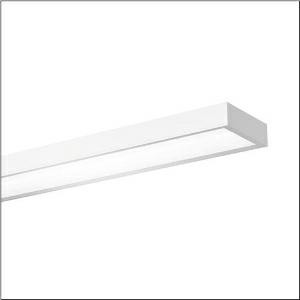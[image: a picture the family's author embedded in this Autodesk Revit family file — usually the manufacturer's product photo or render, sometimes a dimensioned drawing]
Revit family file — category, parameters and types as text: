
# Revit family: sport_31_51hs12dc4dca
name_source: partatom
category: Lighting Fixtures
units: mm (PartAtom-declared; Revit-internal decimal feet)

## family parameters
Cut with Voids When Loaded = No
Host = Face
Light Source = No
Part Type = Normal
Room Calculation Point = No
Round Connector Dimension = Use Diameter
Shared = No

## types (1)
- --- (1 x LED, 8000 lm, 59.4 W, 4000K)
    Apparent Load = 59 VA
    CIE Flux Codes = 65 89 97 100 100
    Color Rendering = 80
    Color Temperature = 4000K
    Default Elevation = 1800 mm
    Description = Sport 31, LED high bay luminaire, primary light control with reflector, of sheet steel, primary anti-glare with prismatic structure, of PC, primary optical cover: cover panel, of PC, light emission: direct distribution, primary light characteristic: symmetric, installation type: suspended mounting, recessed, surface-mounted, LED, rated luminous flux: 8.000lm, luminous efficacy: 135lm/W, light colour: 840, colour temperature: 4000K, control gear: ECG DALI, with terminal, 5-pole, max. 2.5mm², mains connection: 220..240V, AC, 50/60Hz, rated input power: 58W, housing, of sheet steel, traffic white (RAL 9016), length: 1.540mm, width: 315mm, height: 95mm, protection rating (complete): IP20, protection rating (lamp compartment, on room side): IP50, insulation class (complete): insulation class I (protective earthing), certification: CE, ENEC, UKCA, ball protection: ball impact resistant with ceiling mounting or chain suspension, impact resistance: IK08, permissible operating ambient temperature: -20..+35°C, standard: DIN 18032-3, packaging unit: 1 piece
    Height = 100 mm  [stored 0.328084 ft]
    Lamp = 1 x LED
    Lamp Light Flux = 8000 lm
    Lamp Power = 59.4 W
    Lamp count = 1
    Length = 1500 mm
    Luminous efficacy = 135 lm/W
    Manufacturer = Siteco
    ModVariant = No
    Model = 51HS12DC4DCA
    Mounting Place = Ceiling
    Mounting Type = Pendant
    Number of Poles = 1
    OnlyDefault = Yes
    Power Factor = 1
    Product Name = Sport 31
    Product group = LED high bay luminaire
    ProductGroupID = 903
    Protection Class = Protection class I
    Protection Degree = IP 20
    RLX_Detail_Level = 1
    RlxData = <blob elided: 22753 chars, md5=4165faa5>
    Socket = socket
    Standby Power = 0 W
    System Light Flux = 8000 lm
    System Power = 59 W
    Type Comments = factory setting: luminous flux: 100 % | dim-lin: 254 | 247 mA
    Type Image = l_1006823.jpg
    URL = http://relux.com
    VarID = @adj_121141
    Voltage = 0 V
    Weight = 0.00 kg
    Width = 315 mm

note: [stored X ft] marks values corroborated as IEEE doubles in the binary element streams (Revit-internal decimal feet)

## geometry (parser evidence)
native form markers: Blend x4, Sweep x12
no freeform markers — native parametric forms only
